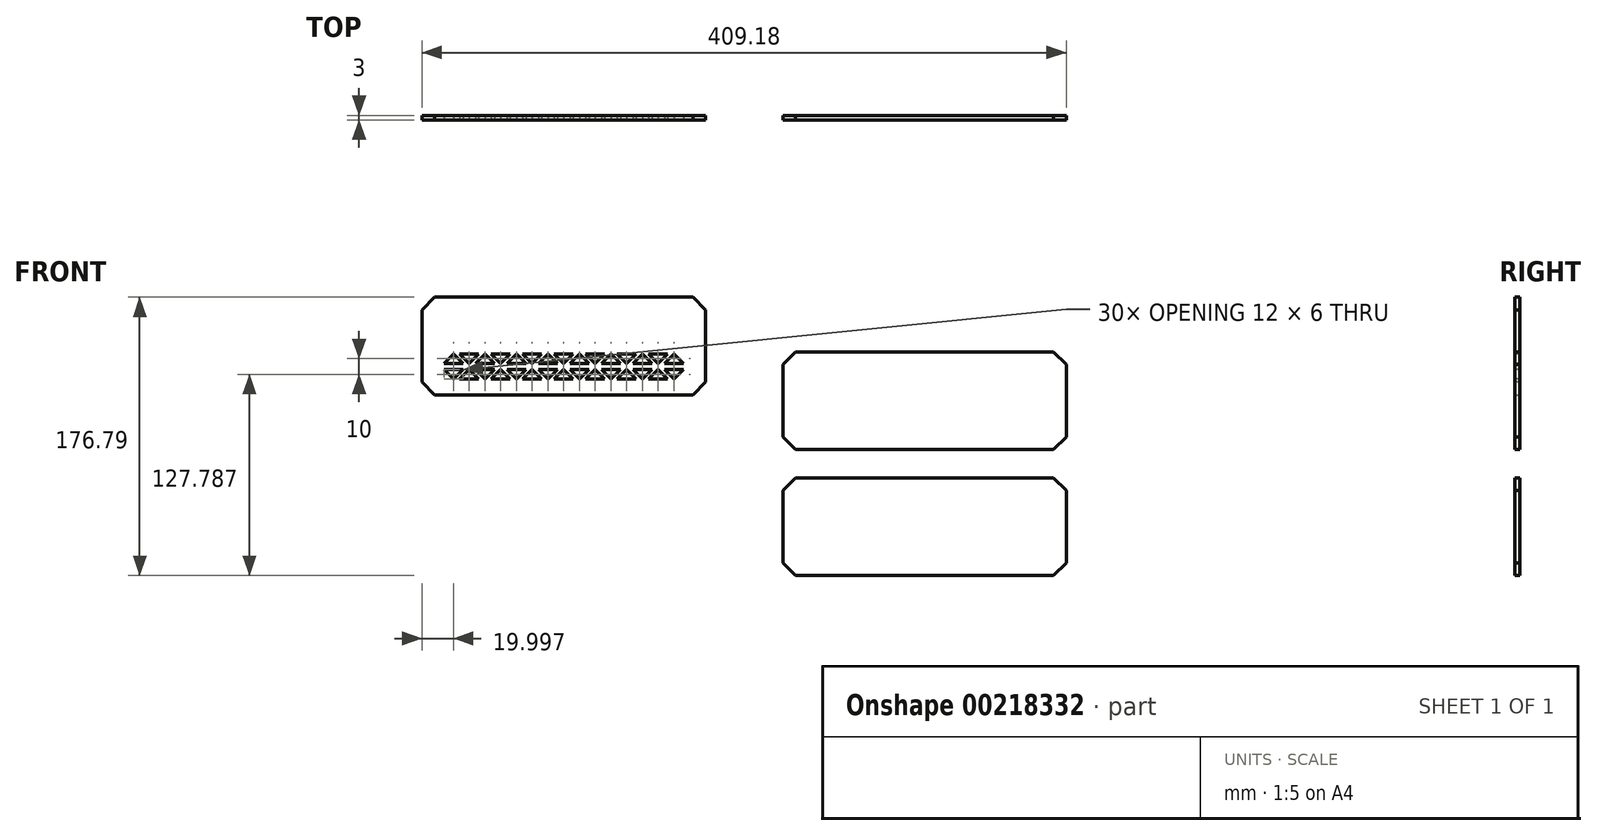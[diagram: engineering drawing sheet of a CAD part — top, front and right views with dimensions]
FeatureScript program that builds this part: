
annotation { "Feature Type Name" : "Feature", "Feature Type Description" : "" }
export const myFeature = defineFeature(function(context is Context, id is Id, definition is map)
    precondition{}
    {
        {
            var Q0;
            Q0=qCreatedBy(makeId("Front.planeOp"),FACE);
            var sketch = newSketch(context, id + "F0", { "sketchPlane" : qUnion([Q0])});
            skLineSegment(sketch, "E0.bottom", {"start": v(-319.18, 65.79) * mm, "end": v(-139.18, 65.79) * mm});
            skLineSegment(sketch, "E0.top", {"start": v(-319.18, 3.79) * mm, "end": v(-139.18, 3.79) * mm});
            skLineSegment(sketch, "E0.left", {"start": v(-319.18, 65.79) * mm, "end": v(-319.18, 3.79) * mm});
            skLineSegment(sketch, "E0.right", {"start": v(-139.18, 65.79) * mm, "end": v(-139.18, 3.79) * mm});
            skSolve(sketch);
        }
        {
            var Q0;
            Q0=makeQuery(id+"F0.imprint","IMPRINT",FACE,{"disambiguationData":[TD([[makeQuery(id+"F0.imprint","IMPRINT",EDGE,{"derivedFrom":sQuery(id+"F0.wireOp",EDGE,"E0.bottom")}),-1.0]])]});
            extrude(context, id + "F1", {"entities" : qUnion([Q0]), "depth" : 3 * mm});
        }
        {
            var Q0;
            Q0=makeQuery(id+"FZRmqtSe0kjUiBv_0.opExtrude","SWEPT_EDGE",EDGE,{"disambiguationData":[OSD([sQuery(id+"FfJ5m6jnL0Aazwi_0.wireOp",EDGE,"JmkRh0oF-DMTZ-ES7a-STX5-WunLXQAGo9QF.bottom"),sQuery(id+"FfJ5m6jnL0Aazwi_0.wireOp",EDGE,"JmkRh0oF-DMTZ-ES7a-STX5-WunLXQAGo9QF.left")])]});
            var Q1;
            Q1=makeQuery(id+"FZRmqtSe0kjUiBv_0.opExtrude","SWEPT_EDGE",EDGE,{"disambiguationData":[OSD([sQuery(id+"FfJ5m6jnL0Aazwi_0.wireOp",EDGE,"JmkRh0oF-DMTZ-ES7a-STX5-WunLXQAGo9QF.top"),sQuery(id+"FfJ5m6jnL0Aazwi_0.wireOp",EDGE,"JmkRh0oF-DMTZ-ES7a-STX5-WunLXQAGo9QF.left")])]});
            var Q2;
            Q2=makeQuery(id+"FZRmqtSe0kjUiBv_0.opExtrude","SWEPT_EDGE",EDGE,{"disambiguationData":[OSD([sQuery(id+"FfJ5m6jnL0Aazwi_0.wireOp",EDGE,"JmkRh0oF-DMTZ-ES7a-STX5-WunLXQAGo9QF.bottom"),sQuery(id+"FfJ5m6jnL0Aazwi_0.wireOp",EDGE,"JmkRh0oF-DMTZ-ES7a-STX5-WunLXQAGo9QF.right")])]});
            var Q3;
            Q3=makeQuery(id+"FZRmqtSe0kjUiBv_0.opExtrude","SWEPT_EDGE",EDGE,{"disambiguationData":[OSD([sQuery(id+"FfJ5m6jnL0Aazwi_0.wireOp",EDGE,"JmkRh0oF-DMTZ-ES7a-STX5-WunLXQAGo9QF.top"),sQuery(id+"FfJ5m6jnL0Aazwi_0.wireOp",EDGE,"JmkRh0oF-DMTZ-ES7a-STX5-WunLXQAGo9QF.right")])]});
            var Q4;
            Q4=makeQuery(id+"F1.opExtrude","SWEPT_EDGE",EDGE,{"disambiguationData":[OSD([sQuery(id+"F0.wireOp",EDGE,"E0.bottom"),sQuery(id+"F0.wireOp",EDGE,"E0.left")])]});
            var Q5;
            Q5=makeQuery(id+"F1.opExtrude","SWEPT_EDGE",EDGE,{"disambiguationData":[OSD([sQuery(id+"F0.wireOp",EDGE,"E0.top"),sQuery(id+"F0.wireOp",EDGE,"E0.left")])]});
            var Q6;
            Q6=makeQuery(id+"F1.opExtrude","SWEPT_EDGE",EDGE,{"disambiguationData":[OSD([sQuery(id+"F0.wireOp",EDGE,"E0.top"),sQuery(id+"F0.wireOp",EDGE,"E0.right")])]});
            var Q7;
            Q7=makeQuery(id+"F1.opExtrude","SWEPT_EDGE",EDGE,{"disambiguationData":[OSD([sQuery(id+"F0.wireOp",EDGE,"E0.bottom"),sQuery(id+"F0.wireOp",EDGE,"E0.right")])]});
            chamfer(context, id + "F2", {"entities" : qUnion([Q0, Q1, Q2, Q3, Q4, Q5, Q6, Q7]), "width" : 8 * mm, "tangentPropagation" : true});
        }
        {
            var Q0;
            Q0=makeQuery(id+"F1.opExtrude","CAP_FACE",FACE,{"disambiguationData":[OSD([sQuery(id+"F0.wireOp",EDGE,"E0.bottom"),sQuery(id+"F0.wireOp",EDGE,"E0.top"),sQuery(id+"F0.wireOp",EDGE,"E0.left"),sQuery(id+"F0.wireOp",EDGE,"E0.right")])],"isStart":false});
            var sketch = newSketch(context, id + "F3", { "sketchPlane" : qUnion([Q0])});
            skLineSegment(sketch, "E1", {"start": v(-319.18, 19.79) * mm, "end": v(-305.18, 19.79) * mm, "construction": true});
            skLineSegment(sketch, "E2", {"start": v(-305.18, 19.79) * mm, "end": v(-293.18, 19.79) * mm});
            skLineSegment(sketch, "E3", {"start": v(-293.18, 19.79) * mm, "end": v(-299.18, 13.79) * mm});
            skLineSegment(sketch, "E4", {"start": v(-299.18, 13.79) * mm, "end": v(-305.18, 19.79) * mm});
            skLineSegment(sketch, "E5", {"start": v(-293.18, 19.79) * mm, "end": v(-289.18, 19.79) * mm, "construction": true});
            skLineSegment(sketch, "E6", {"start": v(-289.18, 19.79) * mm, "end": v(-295.18, 13.79) * mm});
            skLineSegment(sketch, "E7", {"start": v(-295.18, 13.79) * mm, "end": v(-283.18, 13.79) * mm});
            skLineSegment(sketch, "E8", {"start": v(-283.18, 13.79) * mm, "end": v(-289.18, 19.79) * mm});
            skLineSegment(sketch, "E9.1.0.0", {"start": v(-263.18, 13.79) * mm, "end": v(-269.18, 19.79) * mm});
            skLineSegment(sketch, "E9.1.0.1", {"start": v(-269.18, 19.79) * mm, "end": v(-275.18, 13.79) * mm});
            skLineSegment(sketch, "E9.1.0.2", {"start": v(-275.18, 13.79) * mm, "end": v(-263.18, 13.79) * mm});
            skLineSegment(sketch, "E9.1.0.3", {"start": v(-273.18, 19.79) * mm, "end": v(-269.18, 19.79) * mm, "construction": true});
            skLineSegment(sketch, "E9.1.0.4", {"start": v(-285.18, 19.79) * mm, "end": v(-273.18, 19.79) * mm});
            skLineSegment(sketch, "E9.1.0.5", {"start": v(-279.18, 13.79) * mm, "end": v(-285.18, 19.79) * mm});
            skLineSegment(sketch, "E9.1.0.6", {"start": v(-273.18, 19.79) * mm, "end": v(-279.18, 13.79) * mm});
            skLineSegment(sketch, "E9.2.0.0", {"start": v(-243.18, 13.79) * mm, "end": v(-249.18, 19.79) * mm});
            skLineSegment(sketch, "E9.2.0.1", {"start": v(-249.18, 19.79) * mm, "end": v(-255.18, 13.79) * mm});
            skLineSegment(sketch, "E9.2.0.2", {"start": v(-255.18, 13.79) * mm, "end": v(-243.18, 13.79) * mm});
            skLineSegment(sketch, "E9.2.0.3", {"start": v(-253.18, 19.79) * mm, "end": v(-249.18, 19.79) * mm, "construction": true});
            skLineSegment(sketch, "E9.2.0.4", {"start": v(-265.18, 19.79) * mm, "end": v(-253.18, 19.79) * mm});
            skLineSegment(sketch, "E9.2.0.5", {"start": v(-259.18, 13.79) * mm, "end": v(-265.18, 19.79) * mm});
            skLineSegment(sketch, "E9.2.0.6", {"start": v(-253.18, 19.79) * mm, "end": v(-259.18, 13.79) * mm});
            skLineSegment(sketch, "E9.3.0.0", {"start": v(-223.18, 13.79) * mm, "end": v(-229.18, 19.79) * mm});
            skLineSegment(sketch, "E9.3.0.1", {"start": v(-229.18, 19.79) * mm, "end": v(-235.18, 13.79) * mm});
            skLineSegment(sketch, "E9.3.0.2", {"start": v(-235.18, 13.79) * mm, "end": v(-223.18, 13.79) * mm});
            skLineSegment(sketch, "E9.3.0.3", {"start": v(-233.18, 19.79) * mm, "end": v(-229.18, 19.79) * mm, "construction": true});
            skLineSegment(sketch, "E9.3.0.4", {"start": v(-245.18, 19.79) * mm, "end": v(-233.18, 19.79) * mm});
            skLineSegment(sketch, "E9.3.0.5", {"start": v(-239.18, 13.79) * mm, "end": v(-245.18, 19.79) * mm});
            skLineSegment(sketch, "E9.3.0.6", {"start": v(-233.18, 19.79) * mm, "end": v(-239.18, 13.79) * mm});
            skLineSegment(sketch, "E9.4.0.0", {"start": v(-203.18, 13.79) * mm, "end": v(-209.18, 19.79) * mm});
            skLineSegment(sketch, "E9.4.0.1", {"start": v(-209.18, 19.79) * mm, "end": v(-215.18, 13.79) * mm});
            skLineSegment(sketch, "E9.4.0.2", {"start": v(-215.18, 13.79) * mm, "end": v(-203.18, 13.79) * mm});
            skLineSegment(sketch, "E9.4.0.3", {"start": v(-213.18, 19.79) * mm, "end": v(-209.18, 19.79) * mm, "construction": true});
            skLineSegment(sketch, "E9.4.0.4", {"start": v(-225.18, 19.79) * mm, "end": v(-213.18, 19.79) * mm});
            skLineSegment(sketch, "E9.4.0.5", {"start": v(-219.18, 13.79) * mm, "end": v(-225.18, 19.79) * mm});
            skLineSegment(sketch, "E9.4.0.6", {"start": v(-213.18, 19.79) * mm, "end": v(-219.18, 13.79) * mm});
            skLineSegment(sketch, "E9.5.0.0", {"start": v(-183.18, 13.79) * mm, "end": v(-189.18, 19.79) * mm});
            skLineSegment(sketch, "E9.5.0.1", {"start": v(-189.18, 19.79) * mm, "end": v(-195.18, 13.79) * mm});
            skLineSegment(sketch, "E9.5.0.2", {"start": v(-195.18, 13.79) * mm, "end": v(-183.18, 13.79) * mm});
            skLineSegment(sketch, "E9.5.0.3", {"start": v(-193.18, 19.79) * mm, "end": v(-189.18, 19.79) * mm, "construction": true});
            skLineSegment(sketch, "E9.5.0.4", {"start": v(-205.18, 19.79) * mm, "end": v(-193.18, 19.79) * mm});
            skLineSegment(sketch, "E9.5.0.5", {"start": v(-199.18, 13.79) * mm, "end": v(-205.18, 19.79) * mm});
            skLineSegment(sketch, "E9.5.0.6", {"start": v(-193.18, 19.79) * mm, "end": v(-199.18, 13.79) * mm});
            skLineSegment(sketch, "E9.6.0.0", {"start": v(-163.18, 13.79) * mm, "end": v(-169.18, 19.79) * mm});
            skLineSegment(sketch, "E9.6.0.1", {"start": v(-169.18, 19.79) * mm, "end": v(-175.18, 13.79) * mm});
            skLineSegment(sketch, "E9.6.0.2", {"start": v(-175.18, 13.79) * mm, "end": v(-163.18, 13.79) * mm});
            skLineSegment(sketch, "E9.6.0.3", {"start": v(-173.18, 19.79) * mm, "end": v(-169.18, 19.79) * mm, "construction": true});
            skLineSegment(sketch, "E9.6.0.4", {"start": v(-185.18, 19.79) * mm, "end": v(-173.18, 19.79) * mm});
            skLineSegment(sketch, "E9.6.0.5", {"start": v(-179.18, 13.79) * mm, "end": v(-185.18, 19.79) * mm});
            skLineSegment(sketch, "E9.6.0.6", {"start": v(-173.18, 19.79) * mm, "end": v(-179.18, 13.79) * mm});
            skLineSegment(sketch, "E9.direction1", {"start": v(-299.18, 13.79) * mm, "end": v(-279.18, 13.79) * mm, "construction": true});
            skLineSegment(sketch, "E10", {"start": v(-319.18, 23.79) * mm, "end": v(-305.18, 23.79) * mm, "construction": true});
            skLineSegment(sketch, "E11", {"start": v(-305.18, 23.79) * mm, "end": v(-293.18, 23.79) * mm});
            skLineSegment(sketch, "E12", {"start": v(-293.18, 23.79) * mm, "end": v(-299.18, 29.79) * mm});
            skLineSegment(sketch, "E13", {"start": v(-299.18, 29.79) * mm, "end": v(-305.18, 23.79) * mm});
            skLineSegment(sketch, "E14", {"start": v(-293.18, 23.79) * mm, "end": v(-289.18, 23.79) * mm, "construction": true});
            skLineSegment(sketch, "E15", {"start": v(-289.18, 23.79) * mm, "end": v(-295.18, 29.79) * mm});
            skLineSegment(sketch, "E16", {"start": v(-295.18, 29.79) * mm, "end": v(-283.18, 29.79) * mm});
            skLineSegment(sketch, "E17", {"start": v(-283.18, 29.79) * mm, "end": v(-289.18, 23.79) * mm});
            skLineSegment(sketch, "E18.1.0.0", {"start": v(-275.18, 29.79) * mm, "end": v(-263.18, 29.79) * mm});
            skLineSegment(sketch, "E18.1.0.1", {"start": v(-269.18, 23.79) * mm, "end": v(-275.18, 29.79) * mm});
            skLineSegment(sketch, "E18.1.0.2", {"start": v(-273.18, 23.79) * mm, "end": v(-269.18, 23.79) * mm, "construction": true});
            skLineSegment(sketch, "E18.1.0.3", {"start": v(-285.18, 23.79) * mm, "end": v(-273.18, 23.79) * mm});
            skLineSegment(sketch, "E18.1.0.4", {"start": v(-263.18, 29.79) * mm, "end": v(-269.18, 23.79) * mm});
            skLineSegment(sketch, "E18.1.0.5", {"start": v(-273.18, 23.79) * mm, "end": v(-279.18, 29.79) * mm});
            skLineSegment(sketch, "E18.1.0.6", {"start": v(-279.18, 29.79) * mm, "end": v(-285.18, 23.79) * mm});
            skLineSegment(sketch, "E18.1.0.7", {"start": v(-299.18, 23.79) * mm, "end": v(-285.18, 23.79) * mm, "construction": true});
            skLineSegment(sketch, "E18.2.0.0", {"start": v(-255.18, 29.79) * mm, "end": v(-243.18, 29.79) * mm});
            skLineSegment(sketch, "E18.2.0.1", {"start": v(-249.18, 23.79) * mm, "end": v(-255.18, 29.79) * mm});
            skLineSegment(sketch, "E18.2.0.2", {"start": v(-253.18, 23.79) * mm, "end": v(-249.18, 23.79) * mm, "construction": true});
            skLineSegment(sketch, "E18.2.0.3", {"start": v(-265.18, 23.79) * mm, "end": v(-253.18, 23.79) * mm});
            skLineSegment(sketch, "E18.2.0.4", {"start": v(-243.18, 29.79) * mm, "end": v(-249.18, 23.79) * mm});
            skLineSegment(sketch, "E18.2.0.5", {"start": v(-253.18, 23.79) * mm, "end": v(-259.18, 29.79) * mm});
            skLineSegment(sketch, "E18.2.0.6", {"start": v(-259.18, 29.79) * mm, "end": v(-265.18, 23.79) * mm});
            skLineSegment(sketch, "E18.2.0.7", {"start": v(-279.18, 23.79) * mm, "end": v(-265.18, 23.79) * mm, "construction": true});
            skLineSegment(sketch, "E18.3.0.0", {"start": v(-235.18, 29.79) * mm, "end": v(-223.18, 29.79) * mm});
            skLineSegment(sketch, "E18.3.0.1", {"start": v(-229.18, 23.79) * mm, "end": v(-235.18, 29.79) * mm});
            skLineSegment(sketch, "E18.3.0.2", {"start": v(-233.18, 23.79) * mm, "end": v(-229.18, 23.79) * mm, "construction": true});
            skLineSegment(sketch, "E18.3.0.3", {"start": v(-245.18, 23.79) * mm, "end": v(-233.18, 23.79) * mm});
            skLineSegment(sketch, "E18.3.0.4", {"start": v(-223.18, 29.79) * mm, "end": v(-229.18, 23.79) * mm});
            skLineSegment(sketch, "E18.3.0.5", {"start": v(-233.18, 23.79) * mm, "end": v(-239.18, 29.79) * mm});
            skLineSegment(sketch, "E18.3.0.6", {"start": v(-239.18, 29.79) * mm, "end": v(-245.18, 23.79) * mm});
            skLineSegment(sketch, "E18.3.0.7", {"start": v(-259.18, 23.79) * mm, "end": v(-245.18, 23.79) * mm, "construction": true});
            skLineSegment(sketch, "E18.4.0.0", {"start": v(-215.18, 29.79) * mm, "end": v(-203.18, 29.79) * mm});
            skLineSegment(sketch, "E18.4.0.1", {"start": v(-209.18, 23.79) * mm, "end": v(-215.18, 29.79) * mm});
            skLineSegment(sketch, "E18.4.0.2", {"start": v(-213.18, 23.79) * mm, "end": v(-209.18, 23.79) * mm, "construction": true});
            skLineSegment(sketch, "E18.4.0.3", {"start": v(-225.18, 23.79) * mm, "end": v(-213.18, 23.79) * mm});
            skLineSegment(sketch, "E18.4.0.4", {"start": v(-203.18, 29.79) * mm, "end": v(-209.18, 23.79) * mm});
            skLineSegment(sketch, "E18.4.0.5", {"start": v(-213.18, 23.79) * mm, "end": v(-219.18, 29.79) * mm});
            skLineSegment(sketch, "E18.4.0.6", {"start": v(-219.18, 29.79) * mm, "end": v(-225.18, 23.79) * mm});
            skLineSegment(sketch, "E18.4.0.7", {"start": v(-239.18, 23.79) * mm, "end": v(-225.18, 23.79) * mm, "construction": true});
            skLineSegment(sketch, "E18.5.0.0", {"start": v(-195.18, 29.79) * mm, "end": v(-183.18, 29.79) * mm});
            skLineSegment(sketch, "E18.5.0.1", {"start": v(-189.18, 23.79) * mm, "end": v(-195.18, 29.79) * mm});
            skLineSegment(sketch, "E18.5.0.2", {"start": v(-193.18, 23.79) * mm, "end": v(-189.18, 23.79) * mm, "construction": true});
            skLineSegment(sketch, "E18.5.0.3", {"start": v(-205.18, 23.79) * mm, "end": v(-193.18, 23.79) * mm});
            skLineSegment(sketch, "E18.5.0.4", {"start": v(-183.18, 29.79) * mm, "end": v(-189.18, 23.79) * mm});
            skLineSegment(sketch, "E18.5.0.5", {"start": v(-193.18, 23.79) * mm, "end": v(-199.18, 29.79) * mm});
            skLineSegment(sketch, "E18.5.0.6", {"start": v(-199.18, 29.79) * mm, "end": v(-205.18, 23.79) * mm});
            skLineSegment(sketch, "E18.5.0.7", {"start": v(-219.18, 23.79) * mm, "end": v(-205.18, 23.79) * mm, "construction": true});
            skLineSegment(sketch, "E18.6.0.0", {"start": v(-175.18, 29.79) * mm, "end": v(-163.18, 29.79) * mm});
            skLineSegment(sketch, "E18.6.0.1", {"start": v(-169.18, 23.79) * mm, "end": v(-175.18, 29.79) * mm});
            skLineSegment(sketch, "E18.6.0.2", {"start": v(-173.18, 23.79) * mm, "end": v(-169.18, 23.79) * mm, "construction": true});
            skLineSegment(sketch, "E18.6.0.3", {"start": v(-185.18, 23.79) * mm, "end": v(-173.18, 23.79) * mm});
            skLineSegment(sketch, "E18.6.0.4", {"start": v(-163.18, 29.79) * mm, "end": v(-169.18, 23.79) * mm});
            skLineSegment(sketch, "E18.6.0.5", {"start": v(-173.18, 23.79) * mm, "end": v(-179.18, 29.79) * mm});
            skLineSegment(sketch, "E18.6.0.6", {"start": v(-179.18, 29.79) * mm, "end": v(-185.18, 23.79) * mm});
            skLineSegment(sketch, "E18.6.0.7", {"start": v(-199.18, 23.79) * mm, "end": v(-185.18, 23.79) * mm, "construction": true});
            skLineSegment(sketch, "E18.direction1", {"start": v(-319.18, 23.79) * mm, "end": v(-299.18, 23.79) * mm, "construction": true});
            skLineSegment(sketch, "E19", {"start": v(-163.18, 13.79) * mm, "end": v(-159.18, 13.79) * mm, "construction": true});
            skLineSegment(sketch, "E20", {"start": v(-159.18, 13.79) * mm, "end": v(-165.18, 19.79) * mm});
            skLineSegment(sketch, "E21", {"start": v(-165.18, 19.79) * mm, "end": v(-153.18, 19.79) * mm});
            skLineSegment(sketch, "E22", {"start": v(-153.18, 19.79) * mm, "end": v(-159.18, 13.79) * mm});
            skLineSegment(sketch, "E23", {"start": v(-163.18, 29.79) * mm, "end": v(-159.18, 29.79) * mm, "construction": true});
            skLineSegment(sketch, "E24", {"start": v(-159.18, 29.79) * mm, "end": v(-165.18, 23.79) * mm});
            skLineSegment(sketch, "E25", {"start": v(-165.18, 23.79) * mm, "end": v(-153.18, 23.79) * mm});
            skLineSegment(sketch, "E26", {"start": v(-153.18, 23.79) * mm, "end": v(-159.18, 29.79) * mm});
            skSolve(sketch);
        }
        {
            var Q0;
            Q0=qSketchRegion(id+"F3",true);
            extrude(context, id + "F4", {"entities" : qUnion([Q0]), "operationType" : NewBodyOperationType.REMOVE, "oppositeDirection" : true, "depth" : 25 * mm});
        }
        {
            var Q0;
            Q0=qCreatedBy(makeId("Front.planeOp"),FACE);
            var sketch = newSketch(context, id + "F5", { "sketchPlane" : qUnion([Q0])});
            skLineSegment(sketch, "E27.bottom", {"start": v(-90, 31) * mm, "end": v(90, 31) * mm});
            skLineSegment(sketch, "E27.top", {"start": v(-90, -31) * mm, "end": v(90, -31) * mm});
            skLineSegment(sketch, "E27.left", {"start": v(-90, 31) * mm, "end": v(-90, -31) * mm});
            skLineSegment(sketch, "E27.right", {"start": v(90, 31) * mm, "end": v(90, -31) * mm});
            skSolve(sketch);
        }
        {
            var Q0;
            Q0=makeQuery(id+"F5.imprint","IMPRINT",FACE,{"disambiguationData":[TD([[makeQuery(id+"F5.imprint","IMPRINT",EDGE,{"derivedFrom":sQuery(id+"F5.wireOp",EDGE,"E27.bottom")}),-1.0]])]});
            extrude(context, id + "F6", {"entities" : qUnion([Q0]), "depth" : 3 * mm});
        }
        {
            var Q0;
            Q0=makeQuery(id+"F6.opExtrude","SWEPT_EDGE",EDGE,{"disambiguationData":[OSD([sQuery(id+"F5.wireOp",EDGE,"E27.top"),sQuery(id+"F5.wireOp",EDGE,"E27.left")])]});
            var Q1;
            Q1=makeQuery(id+"F6.opExtrude","SWEPT_EDGE",EDGE,{"disambiguationData":[OSD([sQuery(id+"F5.wireOp",EDGE,"E27.bottom"),sQuery(id+"F5.wireOp",EDGE,"E27.left")])]});
            var Q2;
            Q2=makeQuery(id+"F6.opExtrude","SWEPT_EDGE",EDGE,{"disambiguationData":[OSD([sQuery(id+"F5.wireOp",EDGE,"E27.bottom"),sQuery(id+"F5.wireOp",EDGE,"E27.right")])]});
            var Q3;
            Q3=makeQuery(id+"F6.opExtrude","SWEPT_EDGE",EDGE,{"disambiguationData":[OSD([sQuery(id+"F5.wireOp",EDGE,"E27.top"),sQuery(id+"F5.wireOp",EDGE,"E27.right")])]});
            chamfer(context, id + "F7", {"entities" : qUnion([Q0, Q1, Q2, Q3]), "width" : 8 * mm, "tangentPropagation" : true});
        }
        {
            var Q0;
            Q0=makeQuery(id+"F6.opExtrude","SWEPT_BODY",BODY,{"disambiguationData":[OSD([sQuery(id+"F5.wireOp",EDGE,"E27.bottom"),sQuery(id+"F5.wireOp",EDGE,"E27.top"),sQuery(id+"F5.wireOp",EDGE,"E27.left"),sQuery(id+"F5.wireOp",EDGE,"E27.right")])]});
            transform(context, id + "F8", {"entities" : qUnion([Q0]), "transformType" : TransformType.TRANSLATION_3D, "dx" : 0 * mm, "dy" : 0 * mm, "dz" : -80 * mm, "makeCopy" : true});
        }
    });
